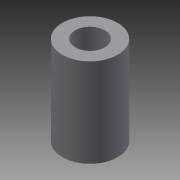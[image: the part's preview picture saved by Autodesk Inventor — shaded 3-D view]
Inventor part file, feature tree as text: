
AUTODESK INVENTOR PART (.ipt)
format: ipt  version: 2013 SP2 (Build 170200200, 200)  size: 72,704 bytes
history: native  units: mm
features: extrude x1, sketch x1
ambient origin geometry x8: Origin, YZ Plane, XZ Plane, XY Plane, X Axis, Y Axis, Z Axis, Center Point
bodies: Solid1 (feature_tree)
feature tree (2):
  extrude  "Extrusion1"  Depth=8.0mm
  sketch  "Sketch1"  dims[d0=15.0mm d2=8.0mm d3=24.0mm d4=0.0mm]
